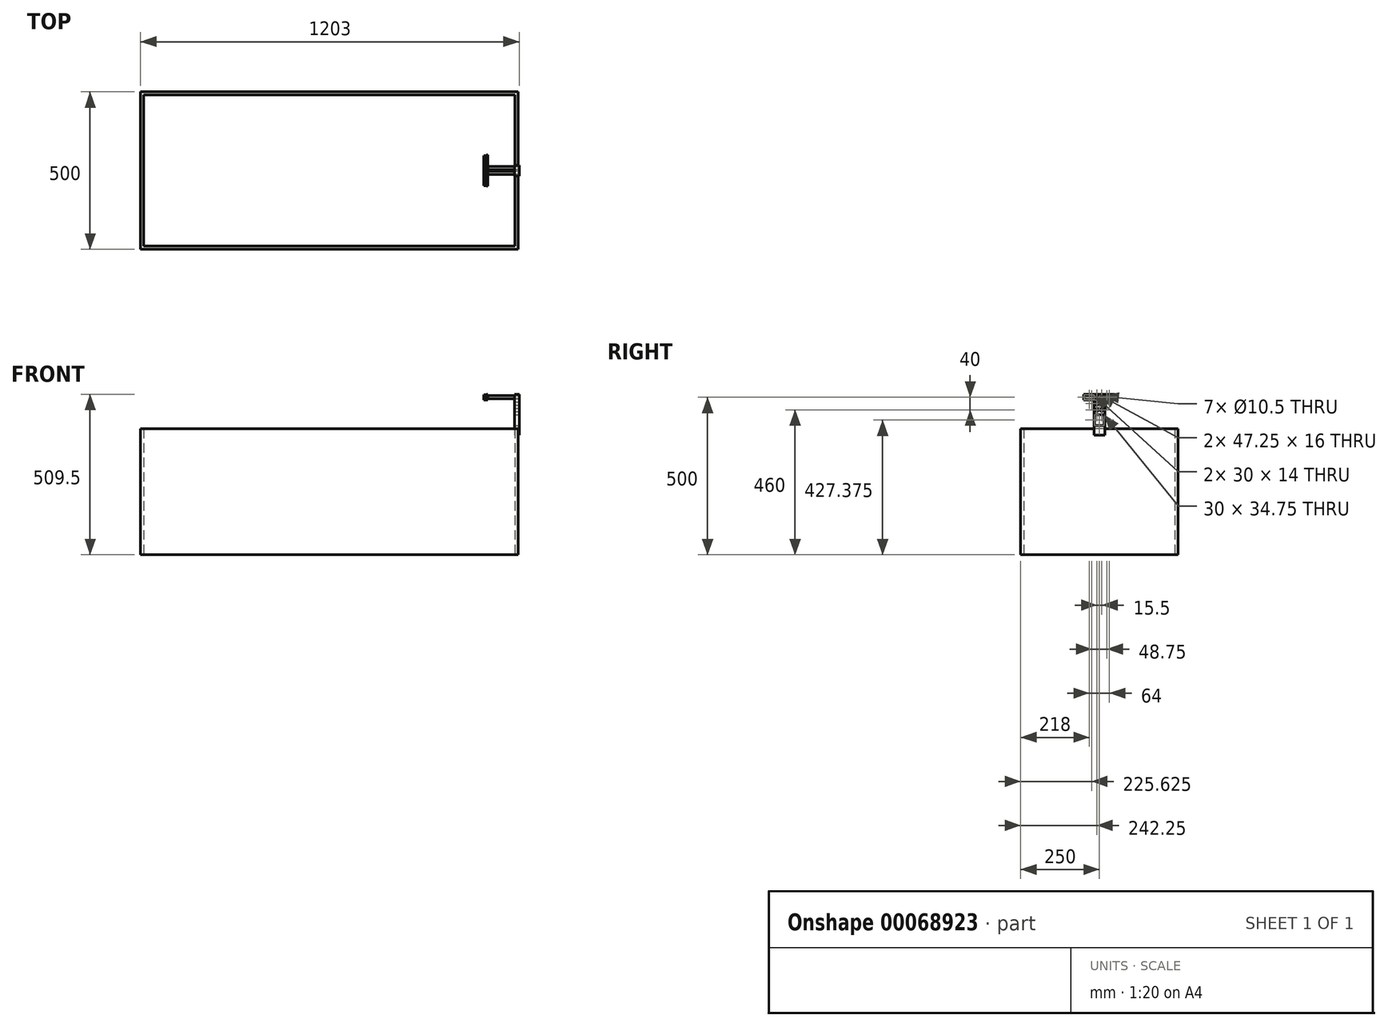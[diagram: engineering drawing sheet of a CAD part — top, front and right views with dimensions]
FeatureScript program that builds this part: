
annotation { "Feature Type Name" : "Feature", "Feature Type Description" : "" }
export const myFeature = defineFeature(function(context is Context, id is Id, definition is map)
    precondition{}
    {
        {
            var Q0;
            Q0=qCreatedBy(makeId("Right.planeOp"),FACE);
            var sketch = newSketch(context, id + "F0", { "sketchPlane" : qUnion([Q0])});
            skLineSegment(sketch, "E0.rect.bottom", {"start": v(-49.5, 9) * mm, "end": v(49.5, 9) * mm});
            skLineSegment(sketch, "E0.rect.top", {"start": v(-49.5, -9) * mm, "end": v(49.5, -9) * mm});
            skLineSegment(sketch, "E0.rect.left", {"start": v(-49.5, 9) * mm, "end": v(-49.5, -9) * mm});
            skLineSegment(sketch, "E0.rect.right", {"start": v(49.5, 9) * mm, "end": v(49.5, -9) * mm});
            skLineSegment(sketch, "E1.bottom", {"start": v(-49.5, -9) * mm, "end": v(0, -9) * mm, "construction": true});
            skLineSegment(sketch, "E1.top", {"start": v(-49.5, 9) * mm, "end": v(0, 9) * mm, "construction": true});
            skLineSegment(sketch, "E2", {"start": v(0, 9) * mm, "end": v(0, -9) * mm, "construction": true});
            skPoint(sketch, "E3.middle", {"position": v(0, 0) * mm});
            skLineSegment(sketch, "E4.bottom", {"start": v(-48, 8) * mm, "end": v(-16, 8) * mm});
            skLineSegment(sketch, "E4.top", {"start": v(-48, -8) * mm, "end": v(-16, -8) * mm});
            skLineSegment(sketch, "E4.left", {"start": v(-48, 8) * mm, "end": v(-48, -8) * mm});
            skLineSegment(sketch, "E5.MirrorCS", {"start": v(48, 8) * mm, "end": v(48, -8) * mm});
            skLineSegment(sketch, "E6.MirrorCS", {"start": v(48, 8) * mm, "end": v(16, 8) * mm});
            skLineSegment(sketch, "E7.MirrorCS", {"start": v(48, -8) * mm, "end": v(16, -8) * mm});
            skLineSegment(sketch, "E8.bottom", {"start": v(50, 9.5) * mm, "end": v(-50, 9.5) * mm});
            skLineSegment(sketch, "E8.top", {"start": v(50, -9.5) * mm, "end": v(-50, -9.5) * mm});
            skLineSegment(sketch, "E8.left", {"start": v(50, 9.5) * mm, "end": v(50, -9.5) * mm});
            skLineSegment(sketch, "E8.right", {"start": v(-50, 9.5) * mm, "end": v(-50, -9.5) * mm});
            skCircle(sketch, "E9", {"center": v(-7.75, 0) * mm, "radius": 5.25 * mm});
            skCircle(sketch, "E10.MirrorC", {"center": v(7.75, 0) * mm, "radius": 5.25 * mm});
            skLineSegment(sketch, "E11.bottom", {"start": v(0.75, 9.5) * mm, "end": v(-0.75, 9.5) * mm});
            skLineSegment(sketch, "E11.top", {"start": v(0.75, -9.5) * mm, "end": v(-0.75, -9.5) * mm});
            skLineSegment(sketch, "E11.left", {"start": v(0.75, 9.5) * mm, "end": v(0.75, -9.5) * mm});
            skLineSegment(sketch, "E11.right", {"start": v(-0.75, 9.5) * mm, "end": v(-0.75, -9.5) * mm});
            skLineSegment(sketch, "E12.0", {"start": v(47, 7) * mm, "end": v(17, 7) * mm});
            skLineSegment(sketch, "E12.1", {"start": v(47, 7) * mm, "end": v(47, -7) * mm});
            skLineSegment(sketch, "E12.2", {"start": v(47, -7) * mm, "end": v(17, -7) * mm});
            skLineSegment(sketch, "E12.3", {"start": v(17, 7) * mm, "end": v(17, -7) * mm});
            skLineSegment(sketch, "E13.MirrorCS", {"start": v(-47, 7) * mm, "end": v(-17, 7) * mm});
            skLineSegment(sketch, "E14.MirrorCS", {"start": v(-17, 7) * mm, "end": v(-17, -7) * mm});
            skLineSegment(sketch, "E15.MirrorCS", {"start": v(-47, -7) * mm, "end": v(-17, -7) * mm});
            skLineSegment(sketch, "E16.MirrorCS", {"start": v(-47, 7) * mm, "end": v(-47, -7) * mm});
            skLineSegment(sketch, "E17.bottom", {"start": v(-13, -8) * mm, "end": v(13, -8) * mm});
            skLineSegment(sketch, "E17.top", {"start": v(-13, 8) * mm, "end": v(13, 8) * mm});
            skLineSegment(sketch, "E18", {"start": v(-16, -8) * mm, "end": v(-13, -8) * mm});
            skLineSegment(sketch, "E19", {"start": v(-16, 8) * mm, "end": v(-13, 8) * mm});
            skLineSegment(sketch, "E20", {"start": v(13, -8) * mm, "end": v(16, -8) * mm});
            skLineSegment(sketch, "E21", {"start": v(13, 8) * mm, "end": v(16, 8) * mm});
            skPoint(sketch, "E3.left.end.orphan", {"position": v(-13, -6) * mm});
            skPoint(sketch, "E22.trimOffspring.start.orphan", {"position": v(-13, 6) * mm});
            skPoint(sketch, "E3.right.end.orphan", {"position": v(13, -6) * mm});
            skPoint(sketch, "E3.right.start.orphan", {"position": v(13, 6) * mm});
            skSolve(sketch);
        }
        {
            var Q0;
            Q0=makeQuery(id+"F0.imprint","IMPRINT",FACE,{"disambiguationData":[TD([[makeQuery(id+"F0.imprint","IMPRINT",EDGE,{"derivedFrom":sQuery(id+"F0.wireOp",EDGE,"E0.rect.bottom")}),-1.0]])]});
            var Q1;
            Q1=makeQuery(id+"F0.imprint","IMPRINT",FACE,{"disambiguationData":[TD([[makeQuery(id+"F0.imprint","IMPRINT",EDGE,{"derivedFrom":sQuery(id+"F0.wireOp",EDGE,"E3.bottom")}),-1.0]])]});
            var Q2;
            {var subQ0=sQuery(id+"F0.wireOp",EDGE,"E11.right");var subQ1=sQuery(id+"F0.wireOp",EDGE,"E0.rect.top");var subQ2=makeQuery(id+"F0.imprint","INTERSECT",VERTEX,{"derivedFrom":[subQ1,subQ0]});Q2=makeQuery(id+"F0.imprint","IMPRINT",FACE,{"disambiguationData":[TD([[makeQuery(id+"F0.imprint","IMPRINT",EDGE,{"disambiguationData":[TD([[subQ2,-1.0]])],"derivedFrom":subQ1}),1.0]])]});}
            var Q3;
            {var subQ4=sQuery(id+"F0.wireOp",EDGE,"E0.rect.right");Q3=makeQuery(id+"F0.imprint","IMPRINT",FACE,{"disambiguationData":[TD([[makeQuery(id+"F0.imprint","IMPRINT",EDGE,{"derivedFrom":subQ4}),-1.0]])]});}
            var Q4;
            {var subQ0=sQuery(id+"F0.wireOp",EDGE,"E3.right");Q4=makeQuery(id+"F0.imprint","IMPRINT",FACE,{"disambiguationData":[TD([[makeQuery(id+"F0.imprint","IMPRINT",EDGE,{"derivedFrom":subQ0}),-1.0]])]});}
            var Q5;
            {var subQ5=sQuery(id+"F0.wireOp",EDGE,"E3.left");Q5=makeQuery(id+"F0.imprint","IMPRINT",FACE,{"disambiguationData":[TD([[makeQuery(id+"F0.imprint","IMPRINT",EDGE,{"derivedFrom":subQ5}),1.0]])]});}
            var Q6;
            {var subQ0=sQuery(id+"F0.wireOp",EDGE,"E0.rect.left");Q6=makeQuery(id+"F0.imprint","IMPRINT",FACE,{"disambiguationData":[TD([[makeQuery(id+"F0.imprint","IMPRINT",EDGE,{"derivedFrom":subQ0}),1.0]])]});}
            var Q7;
            {var subQ0=sQuery(id+"F0.wireOp",EDGE,"E17.top");var subQ1=sQuery(id+"F0.wireOp",EDGE,"E11.left");var subQ2=makeQuery(id+"F0.imprint","INTERSECT",VERTEX,{"derivedFrom":[subQ1,subQ0]});Q7=makeQuery(id+"F0.imprint","IMPRINT",FACE,{"disambiguationData":[TD([[makeQuery(id+"F0.imprint","IMPRINT",EDGE,{"disambiguationData":[TD([[subQ2,-1.0]])],"derivedFrom":subQ1}),-1.0]])]});}
            var Q8;
            Q8=makeQuery(id+"F0.imprint","IMPRINT",FACE,{"disambiguationData":[TD([[makeQuery(id+"F0.imprint","IMPRINT",EDGE,{"derivedFrom":sQuery(id+"F0.wireOp",EDGE,"E10.MirrorC")}),1.0]])]});
            extrude(context, id + "F1", {"entities" : qUnion([Q0, Q1, Q2, Q3, Q4, Q5, Q6, Q7, Q8]), "depth" : 3 * mm});
        }
        {
            var Q0;
            Q0=makeQuery(id+"F0.imprint","IMPRINT",FACE,{"disambiguationData":[TD([[makeQuery(id+"F0.imprint","IMPRINT",EDGE,{"derivedFrom":sQuery(id+"F0.wireOp",EDGE,"E4.bottom")}),-1.0]])]});
            var Q1;
            Q1=makeQuery(id+"F0.imprint","IMPRINT",FACE,{"disambiguationData":[TD([[makeQuery(id+"F0.imprint","IMPRINT",EDGE,{"derivedFrom":sQuery(id+"F0.wireOp",EDGE,"E5.MirrorCS")}),-1.0]])]});
            var Q2;
            {var subQ0=sQuery(id+"F0.wireOp",EDGE,"E3.right");Q2=makeQuery(id+"F0.imprint","IMPRINT",FACE,{"disambiguationData":[TD([[makeQuery(id+"F0.imprint","IMPRINT",EDGE,{"derivedFrom":subQ0}),-1.0]])]});}
            var Q3;
            {var subQ5=sQuery(id+"F0.wireOp",EDGE,"E3.left");Q3=makeQuery(id+"F0.imprint","IMPRINT",FACE,{"disambiguationData":[TD([[makeQuery(id+"F0.imprint","IMPRINT",EDGE,{"derivedFrom":subQ5}),1.0]])]});}
            var Q4;
            Q4=makeQuery(id+"F0.imprint","IMPRINT",FACE,{"disambiguationData":[TD([[makeQuery(id+"F0.imprint","IMPRINT",EDGE,{"derivedFrom":sQuery(id+"F0.wireOp",EDGE,"E10.MirrorC")}),1.0]])]});
            extrude(context, id + "F2", {"entities" : qUnion([Q0, Q1, Q2, Q3, Q4]), "operationType" : NewBodyOperationType.ADD, "oppositeDirection" : true, "depth" : 10 * mm, "hasSecondDirection" : true, "secondDirectionOppositeDirection" : false, "secondDirectionDepth" : 2 * mm});
        }
        {
            var Q0;
            Q0=qSketchRegion(id+"F0",true);
            var Q1;
            Q1=sQuery(id+"F0.wireOp",EDGE,"E8.right");
            var Q2;
            Q2=sQuery(id+"F0.wireOp",EDGE,"E8.top");
            var Q3;
            Q3=sQuery(id+"F0.wireOp",EDGE,"E8.left");
            var Q4;
            Q4=sQuery(id+"F0.wireOp",EDGE,"E8.bottom");
            extrude(context, id + "F3", {"entities" : qUnion([Q0]), "bodyType" : ToolBodyType.SURFACE, "surfaceEntities" : qUnion([Q1, Q2, Q3, Q4]), "oppositeDirection" : true, "depth" : 1000 * mm});
        }
        {
            var Q0;
            Q0=qCreatedBy(makeId("Top.planeOp"),FACE);
            cPlane(context, id + "F4", {"entities" : qUnion([Q0]), "cplaneType" : CPlaneType.OFFSET, "offset" : 500 * mm, "oppositeDirection" : true, "width" : 150 * mm, "height" : 150 * mm});
        }
        {
            var Q0;
            Q0=qCreatedBy(id+"F4.planeOp",FACE);
            var sketch = newSketch(context, id + "F5", { "sketchPlane" : qUnion([Q0])});
            skLineSegment(sketch, "E23.0", {"start": v(-1100, 250) * mm, "end": v(100, 250) * mm});
            skLineSegment(sketch, "E24.0", {"start": v(-1090, 240) * mm, "end": v(-1090, -240) * mm});
            skLineSegment(sketch, "E25.0", {"start": v(-1100, 250) * mm, "end": v(-1100, -250) * mm});
            skLineSegment(sketch, "E26.0", {"start": v(-1100, -250) * mm, "end": v(100, -250) * mm});
            skLineSegment(sketch, "E27.0", {"start": v(-1090, -240) * mm, "end": v(90, -240) * mm});
            skLineSegment(sketch, "E28.0", {"start": v(100, 250) * mm, "end": v(100, -250) * mm});
            skLineSegment(sketch, "E29.0", {"start": v(90, 240) * mm, "end": v(90, -240) * mm});
            skLineSegment(sketch, "E30.0", {"start": v(-1090, 240) * mm, "end": v(90, 240) * mm});
            skSolve(sketch);
        }
        {
            var Q0;
            Q0=qSketchRegion(id+"F5",true);
            extrude(context, id + "F6", {"entities" : qUnion([Q0]), "depth" : 400 * mm});
        }
        {
            var Q0;
            Q0=makeQuery(id+"F6.opExtrude","CAP_FACE",FACE,{"disambiguationData":[OSD([sQuery(id+"F5.wireOp",EDGE,"E23.0"),sQuery(id+"F5.wireOp",EDGE,"E24.0"),sQuery(id+"F5.wireOp",EDGE,"E25.0"),sQuery(id+"F5.wireOp",EDGE,"E26.0"),sQuery(id+"F5.wireOp",EDGE,"E27.0"),sQuery(id+"F5.wireOp",EDGE,"E28.0"),sQuery(id+"F5.wireOp",EDGE,"E29.0"),sQuery(id+"F5.wireOp",EDGE,"E30.0")])],"isStart":false});
            var sketch = newSketch(context, id + "F7", { "sketchPlane" : qUnion([Q0])});
            skLineSegment(sketch, "E31", {"start": v(0, 15) * mm, "end": v(90, 15) * mm, "construction": true});
            skLineSegment(sketch, "E32", {"start": v(0, -15) * mm, "end": v(90, -15) * mm, "construction": true});
            skLineSegment(sketch, "E33.bottom", {"start": v(90, 15) * mm, "end": v(101, 15) * mm});
            skLineSegment(sketch, "E33.top", {"start": v(90, -15) * mm, "end": v(101, -15) * mm});
            skLineSegment(sketch, "E33.left", {"start": v(90, 15) * mm, "end": v(90, -15) * mm});
            skLineSegment(sketch, "E33.right", {"start": v(101, 15) * mm, "end": v(101, -15) * mm});
            skLineSegment(sketch, "E34.0", {"start": v(88, 17) * mm, "end": v(103, 17) * mm});
            skLineSegment(sketch, "E34.1", {"start": v(88, 17) * mm, "end": v(88, -17) * mm});
            skLineSegment(sketch, "E34.2", {"start": v(88, -17) * mm, "end": v(103, -17) * mm});
            skLineSegment(sketch, "E34.3", {"start": v(103, 17) * mm, "end": v(103, -17) * mm});
            skLineSegment(sketch, "E35", {"start": v(90, 15) * mm, "end": v(90, 17) * mm});
            skLineSegment(sketch, "E36", {"start": v(101, 15) * mm, "end": v(101, 17) * mm});
            skLineSegment(sketch, "E37", {"start": v(90, -15) * mm, "end": v(90, -17) * mm});
            skLineSegment(sketch, "E38", {"start": v(101, -15) * mm, "end": v(101, -17) * mm});
            skLineSegment(sketch, "E39", {"start": v(0, 0) * mm, "end": v(105.96, 0) * mm, "construction": true});
            skLineSegment(sketch, "E40", {"start": v(103, 0) * mm, "end": v(88, 0) * mm, "construction": true});
            skSolve(sketch);
        }
        {
            var Q0;
            Q0=makeQuery(id+"F7.imprint","IMPRINT",FACE,{"disambiguationData":[TD([[makeQuery(id+"F7.imprint","IMPRINT",EDGE,{"derivedFrom":sQuery(id+"F7.wireOp",EDGE,"E33.right")}),1.0]])]});
            var Q1;
            Q1=makeQuery(id+"F7.imprint","IMPRINT",FACE,{"disambiguationData":[TD([[makeQuery(id+"F7.imprint","IMPRINT",EDGE,{"derivedFrom":sQuery(id+"F7.wireOp",EDGE,"E33.left")}),-1.0]])]});
            var Q2;
            {var subQ0=sQuery(id+"F7.wireOp",EDGE,"E35");Q2=makeQuery(id+"F7.imprint","IMPRINT",FACE,{"disambiguationData":[TD([[makeQuery(id+"F7.imprint","IMPRINT",EDGE,{"derivedFrom":subQ0}),1.0]])]});}
            var Q3;
            {var subQ0=sQuery(id+"F7.wireOp",EDGE,"E36");Q3=makeQuery(id+"F7.imprint","IMPRINT",FACE,{"disambiguationData":[TD([[makeQuery(id+"F7.imprint","IMPRINT",EDGE,{"derivedFrom":subQ0}),1.0]])]});}
            var Q4;
            {var subQ0=sQuery(id+"F7.wireOp",EDGE,"E38");Q4=makeQuery(id+"F7.imprint","IMPRINT",FACE,{"disambiguationData":[TD([[makeQuery(id+"F7.imprint","IMPRINT",EDGE,{"derivedFrom":subQ0}),-1.0]])]});}
            var Q5;
            {var subQ0=sQuery(id+"F7.wireOp",EDGE,"E37");Q5=makeQuery(id+"F7.imprint","IMPRINT",FACE,{"disambiguationData":[TD([[makeQuery(id+"F7.imprint","IMPRINT",EDGE,{"derivedFrom":subQ0}),1.0]])]});}
            var Q6;
            {var subQ0=sQuery(id+"F7.wireOp",EDGE,"E33.right");Q6=makeQuery(id+"F7.imprint","IMPRINT",FACE,{"disambiguationData":[TD([[makeQuery(id+"F7.imprint","IMPRINT",EDGE,{"derivedFrom":subQ0}),-1.0]])]});}
            var Q7;
            {var subQ0=sQuery(id+"F7.wireOp",EDGE,"E33.left");Q7=makeQuery(id+"F7.imprint","IMPRINT",FACE,{"disambiguationData":[TD([[makeQuery(id+"F7.imprint","IMPRINT",EDGE,{"derivedFrom":subQ0}),1.0]])]});}
            extrude(context, id + "F8", {"entities" : qUnion([Q0, Q1, Q2, Q3, Q4, Q5, Q6, Q7]), "depth" : 10 * mm});
        }
        {
            var Q0;
            Q0=makeQuery(id+"F7.imprint","IMPRINT",FACE,{"disambiguationData":[TD([[makeQuery(id+"F7.imprint","IMPRINT",EDGE,{"derivedFrom":sQuery(id+"F7.wireOp",EDGE,"E33.left")}),-1.0]])]});
            var Q1;
            Q1=makeQuery(id+"F7.imprint","IMPRINT",FACE,{"disambiguationData":[TD([[makeQuery(id+"F7.imprint","IMPRINT",EDGE,{"derivedFrom":sQuery(id+"F7.wireOp",EDGE,"E33.right")}),1.0]])]});
            extrude(context, id + "F9", {"entities" : qUnion([Q0, Q1]), "operationType" : NewBodyOperationType.ADD, "oppositeDirection" : true, "depth" : 20 * mm});
        }
        {
            var Q0;
            {var subQ0=sQuery(id+"F7.wireOp",EDGE,"E34.3");Q0=makeQuery(id+"F9.boolean.opBoolean","MERGE",FACE,{"derivedFrom":[makeQuery(id+"F8.opExtrude","SWEPT_FACE",FACE,{"disambiguationData":[OSD([subQ0])]}),makeQuery(id+"F9.opExtrude","SWEPT_FACE",FACE,{"disambiguationData":[OSD([subQ0])]})]});}
            var sketch = newSketch(context, id + "F10", { "sketchPlane" : qUnion([Q0])});
            skLineSegment(sketch, "E41.0", {"start": v(-17, -90) * mm, "end": v(-17, -120) * mm});
            skLineSegment(sketch, "E42.0", {"start": v(17, -90) * mm, "end": v(17, -120) * mm});
            skLineSegment(sketch, "E43.0", {"start": v(17, -90) * mm, "end": v(-17, -90) * mm});
            skLineSegment(sketch, "E44.0", {"start": v(17, -100) * mm, "end": v(-17, -100) * mm});
            skCircle(sketch, "E45.0", {"center": v(-7.75, 0) * mm, "radius": 5.25 * mm});
            skCircle(sketch, "E46.0", {"center": v(7.75, 0) * mm, "radius": 5.25 * mm});
            skLineSegment(sketch, "E47.bottom", {"start": v(-17, -90) * mm, "end": v(17, -90) * mm});
            skLineSegment(sketch, "E47.top", {"start": v(-17, 9.5) * mm, "end": v(17, 9.5) * mm});
            skLineSegment(sketch, "E47.left", {"start": v(-17, -90) * mm, "end": v(-17, 9.5) * mm});
            skLineSegment(sketch, "E47.right", {"start": v(17, -90) * mm, "end": v(17, 9.5) * mm});
            skLineSegment(sketch, "E48", {"start": v(-9.98, -10) * mm, "end": v(10.55, -10) * mm, "construction": true});
            skCircle(sketch, "E49.MirrorC", {"center": v(-7.75, -20) * mm, "radius": 5.25 * mm});
            skCircle(sketch, "E50.MirrorC", {"center": v(7.75, -20) * mm, "radius": 5.25 * mm});
            skLineSegment(sketch, "E51", {"start": v(-9.28, -30) * mm, "end": v(11.94, -30) * mm});
            skCircle(sketch, "E52.MirrorC", {"center": v(7.75, -40) * mm, "radius": 5.25 * mm});
            skCircle(sketch, "E53.MirrorC", {"center": v(-7.75, -40) * mm, "radius": 5.25 * mm});
            skLineSegment(sketch, "E54.bottom", {"start": v(-15, -55.25) * mm, "end": v(15, -55.25) * mm});
            skLineSegment(sketch, "E54.top", {"start": v(-15, -90) * mm, "end": v(15, -90) * mm});
            skLineSegment(sketch, "E54.left", {"start": v(-15, -55.25) * mm, "end": v(-15, -90) * mm});
            skLineSegment(sketch, "E54.right", {"start": v(15, -55.25) * mm, "end": v(15, -90) * mm});
            skLineSegment(sketch, "E55.0", {"start": v(50, 9.5) * mm, "end": v(-50, 9.5) * mm});
            skSolve(sketch);
        }
        {
            var Q0;
            Q0=qSketchRegion(id+"F10",true);
            var Q1;
            Q1=makeQuery(id+"F10.imprint","IMPRINT",FACE,{"disambiguationData":[TD([[makeQuery(id+"F10.imprint","IMPRINT",EDGE,{"derivedFrom":sQuery(id+"F10.wireOp",EDGE,"E45.0")}),-1.0]])]});
            extrude(context, id + "F11", {"entities" : qUnion([Q0, Q1]), "operationType" : NewBodyOperationType.ADD, "oppositeDirection" : true, "depth" : 15 * mm});
        }
        {
            var Q0;
            Q0=qCreatedBy(makeId("Top.planeOp"),FACE);
            var sketch = newSketch(context, id + "F12", { "sketchPlane" : qUnion([Q0])});
            skLineSegment(sketch, "E56.bottom", {"start": v(-7, -2.5) * mm, "end": v(103, -2.5) * mm});
            skLineSegment(sketch, "E56.top", {"start": v(-7, -7.5) * mm, "end": v(103, -7.5) * mm});
            skLineSegment(sketch, "E56.left", {"start": v(-7, -2.5) * mm, "end": v(-7, -7.5) * mm});
            skLineSegment(sketch, "E56.right", {"start": v(103, -2.5) * mm, "end": v(103, -7.5) * mm});
            skLineSegment(sketch, "E57", {"start": v(0, 0) * mm, "end": v(122.29, 0) * mm, "construction": true});
            skLineSegment(sketch, "E58.MirrorCS", {"start": v(-7, 2.5) * mm, "end": v(-7, 7.5) * mm});
            skLineSegment(sketch, "E59.MirrorCS", {"start": v(103, 2.5) * mm, "end": v(103, 7.5) * mm});
            skLineSegment(sketch, "E60.MirrorCS", {"start": v(-7, 7.5) * mm, "end": v(103, 7.5) * mm});
            skLineSegment(sketch, "E61.MirrorCS", {"start": v(-7, 2.5) * mm, "end": v(103, 2.5) * mm});
            skLineSegment(sketch, "E62.0", {"start": v(103, 2.5) * mm, "end": v(103, 13) * mm});
            skLineSegment(sketch, "E63.0", {"start": v(103, -2.5) * mm, "end": v(103, -13) * mm});
            skSolve(sketch);
        }
        {
            var Q0;
            Q0=makeQuery(id+"F12.imprint","IMPRINT",FACE,{"disambiguationData":[TD([[makeQuery(id+"F12.imprint","IMPRINT",EDGE,{"derivedFrom":sQuery(id+"F12.wireOp",EDGE,"E56.bottom")}),-1.0]])]});
            var Q1;
            Q1=sQuery(id+"F12.wireOp",EDGE,"E56.top");
            revolve(context, id + "F13", {"entities" : qUnion([Q0]), "axis" : qUnion([Q1]), "revolveType" : RevolveType.FULL});
        }
        {
            var Q0;
            Q0=makeQuery(id+"F12.imprint","IMPRINT",FACE,{"disambiguationData":[TD([[makeQuery(id+"F12.imprint","IMPRINT",EDGE,{"derivedFrom":sQuery(id+"F12.wireOp",EDGE,"E59.MirrorCS")}),1.0]])]});
            var Q1;
            {var subQ0=sQuery(id+"F12.wireOp",EDGE,"E58.MirrorCS");Q1=makeQuery(id+"F12.imprint","IMPRINT",FACE,{"disambiguationData":[TD([[makeQuery(id+"F12.imprint","IMPRINT",EDGE,{"derivedFrom":subQ0}),-1.0]])]});}
            var Q2;
            Q2=sQuery(id+"F12.wireOp",EDGE,"E60.MirrorCS");
            revolve(context, id + "F14", {"entities" : qUnion([Q0, Q1]), "axis" : qUnion([Q2]), "revolveType" : RevolveType.FULL});
        }
    });
